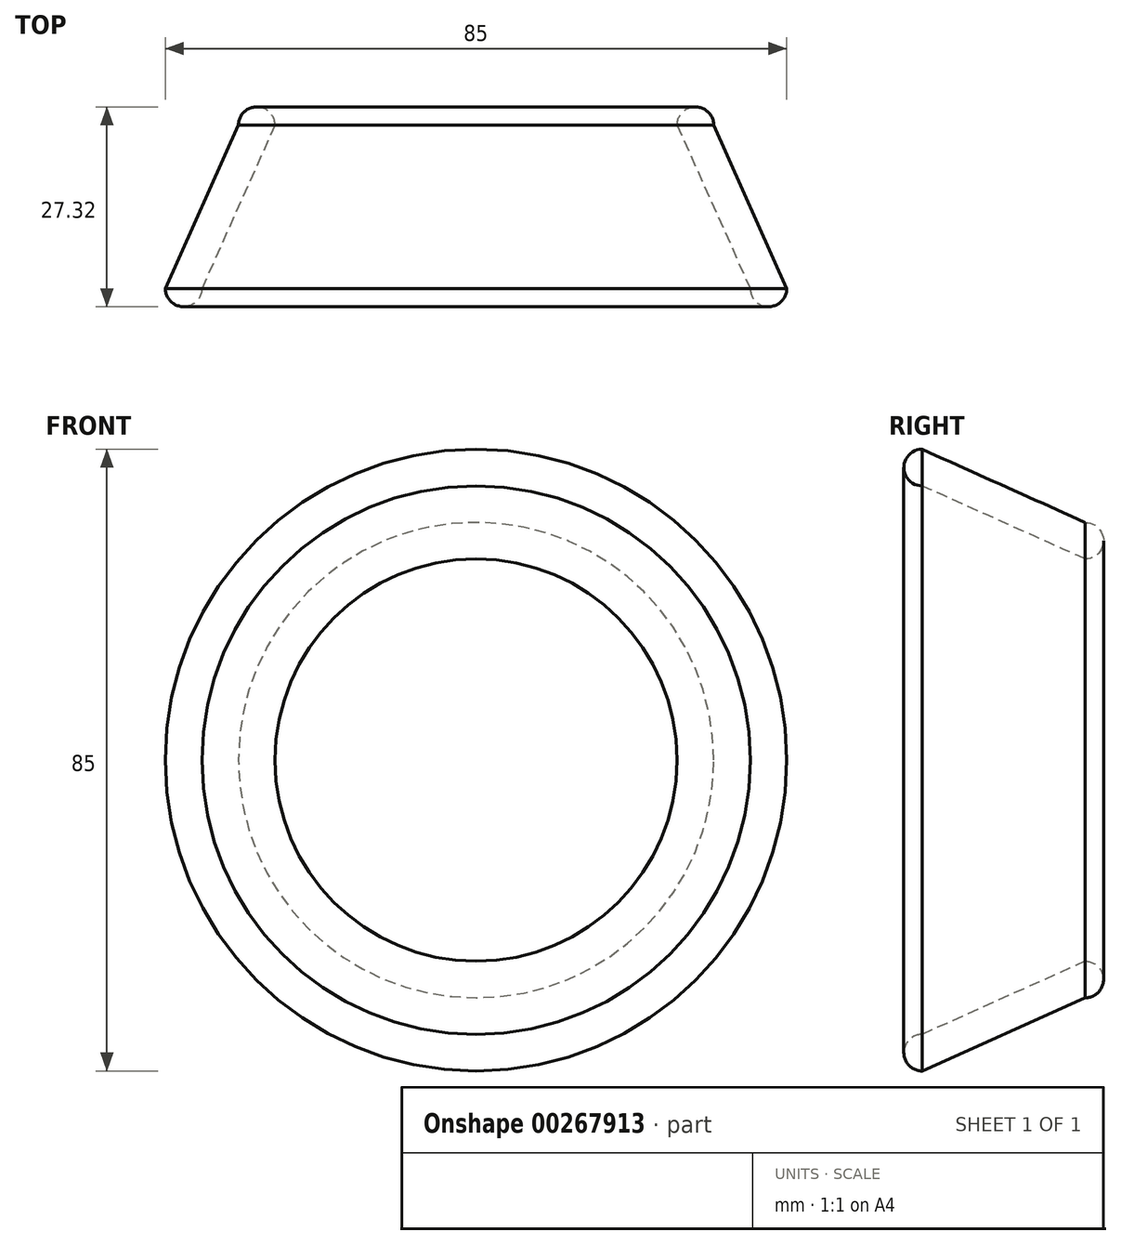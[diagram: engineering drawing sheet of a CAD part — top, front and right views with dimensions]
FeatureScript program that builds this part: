
annotation { "Feature Type Name" : "Feature", "Feature Type Description" : "" }
export const myFeature = defineFeature(function(context is Context, id is Id, definition is map)
    precondition{}
    {
        {
            var Q0;
            Q0=qCreatedBy(makeId("Top.planeOp"),FACE);
            var sketch = newSketch(context, id + "F0", { "sketchPlane" : qUnion([Q0])});
            skLineSegment(sketch, "E0", {"start": v(0, 0) * mm, "end": v(-30, 0) * mm});
            skLineSegment(sketch, "E1", {"start": v(0, 0) * mm, "end": v(30, 0) * mm});
            skLineSegment(sketch, "E2", {"start": v(0, 0) * mm, "end": v(0, -5) * mm});
            skLineSegment(sketch, "E3", {"start": v(0, -5) * mm, "end": v(0, -22.32) * mm});
            skLineSegment(sketch, "E4", {"start": v(0, -22.32) * mm, "end": v(0, -27.32) * mm});
            skLineSegment(sketch, "E5", {"start": v(0, -27.32) * mm, "end": v(40, -27.32) * mm});
            skLineSegment(sketch, "E6", {"start": v(0, -27.32) * mm, "end": v(-40, -27.32) * mm});
            skLineSegment(sketch, "E7", {"start": v(-32.5, -2.5) * mm, "end": v(-42.5, -24.82) * mm});
            skLineSegment(sketch, "E8", {"start": v(-37.5, -24.82) * mm, "end": v(-27.5, -2.5) * mm});
            skLineSegment(sketch, "E9", {"start": v(32.5, -2.5) * mm, "end": v(42.5, -24.82) * mm});
            skLineSegment(sketch, "E10", {"start": v(37.5, -24.82) * mm, "end": v(27.5, -2.5) * mm});
            skLineSegment(sketch, "E11", {"start": v(0, -22.32) * mm, "end": v(41.38, -22.32) * mm});
            skLineSegment(sketch, "E12", {"start": v(0, -22.32) * mm, "end": v(-41.38, -22.32) * mm});
            skLineSegment(sketch, "E13", {"start": v(0, -5) * mm, "end": v(33.62, -5) * mm});
            skLineSegment(sketch, "E14", {"start": v(0, -5) * mm, "end": v(-33.62, -5) * mm});
            skArc(sketch, "E15", {"start": v(-27.5, -2.5) * mm, "mid": v(-30, 0) * mm, "end": v(-32.5, -2.5) * mm});
            skArc(sketch, "E16", {"start": v(32.5, -2.5) * mm, "mid": v(30, 0) * mm, "end": v(27.5, -2.5) * mm});
            skArc(sketch, "E17", {"start": v(37.5, -24.82) * mm, "mid": v(40, -27.32) * mm, "end": v(42.5, -24.82) * mm});
            skArc(sketch, "E18", {"start": v(-42.5, -24.82) * mm, "mid": v(-40, -27.32) * mm, "end": v(-37.5, -24.82) * mm});
            skSolve(sketch);
        }
        {
            var Q0;
            {var subQ1=sQuery(id+"F0.wireOp",EDGE,"E7");var subQ5=sQuery(id+"F0.wireOp",EDGE,"E15");var subQ8=makeQuery(id+"F0.imprint","INTERSECT",VERTEX,{"derivedFrom":[subQ1,subQ5]});Q0=makeQuery(id+"F0.imprint","IMPRINT",FACE,{"disambiguationData":[TD([[makeQuery(id+"F0.imprint","IMPRINT",EDGE,{"disambiguationData":[TD([[subQ8,-1.0]])],"derivedFrom":subQ1}),1.0]])]});}
            var Q1;
            {var subQ0=sQuery(id+"F0.wireOp",EDGE,"E12");var subQ1=sQuery(id+"F0.wireOp",EDGE,"E7");var subQ2=makeQuery(id+"F0.imprint","INTERSECT",VERTEX,{"derivedFrom":[subQ1,subQ0]});Q1=makeQuery(id+"F0.imprint","IMPRINT",FACE,{"disambiguationData":[TD([[makeQuery(id+"F0.imprint","IMPRINT",EDGE,{"disambiguationData":[TD([[subQ2,1.0]])],"derivedFrom":subQ1}),1.0]])]});}
            var Q2;
            {var subQ0=sQuery(id+"F0.wireOp",EDGE,"E18");var subQ2=sQuery(id+"F0.wireOp",EDGE,"E7");var subQ3=makeQuery(id+"F0.imprint","INTERSECT",VERTEX,{"derivedFrom":[subQ2,subQ0]});Q2=makeQuery(id+"F0.imprint","IMPRINT",FACE,{"disambiguationData":[TD([[makeQuery(id+"F0.imprint","IMPRINT",EDGE,{"disambiguationData":[TD([[subQ3,1.0]])],"derivedFrom":subQ2}),1.0]])]});}
            var Q3;
            Q3=sQuery(id+"F0.wireOp",EDGE,"E3");
            revolve(context, id + "F1", {"entities" : qUnion([Q0, Q1, Q2]), "axis" : qUnion([Q3]), "revolveType" : RevolveType.FULL});
        }
    });
